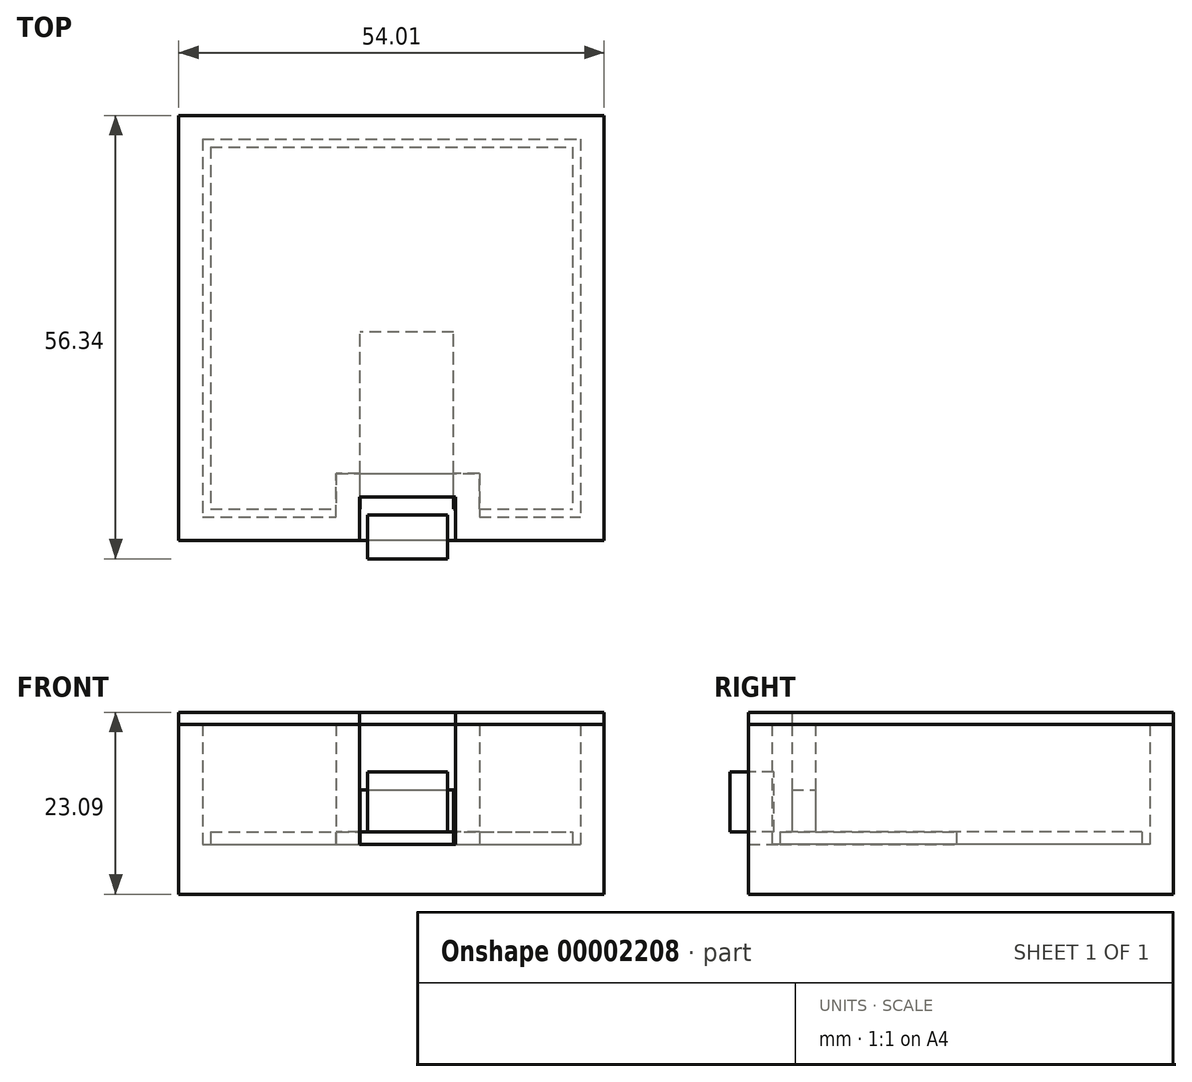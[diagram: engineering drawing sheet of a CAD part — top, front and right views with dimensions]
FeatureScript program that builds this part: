
annotation { "Feature Type Name" : "Feature", "Feature Type Description" : "" }
export const myFeature = defineFeature(function(context is Context, id is Id, definition is map)
    precondition{}
    {
        {
            var Q0;
            Q0=qCreatedBy(makeId("Top.planeOp"),FACE);
            var sketch = newSketch(context, id + "F0", { "sketchPlane" : qUnion([Q0])});
            skLineSegment(sketch, "E0.bottom", {"start": v(-26.57, 18.84) * mm, "end": v(19.4, 18.84) * mm});
            skLineSegment(sketch, "E0.top", {"start": v(-26.57, -27.13) * mm, "end": v(19.4, -27.13) * mm});
            skLineSegment(sketch, "E0.left", {"start": v(-26.57, 18.84) * mm, "end": v(-26.57, -27.13) * mm});
            skLineSegment(sketch, "E0.right", {"start": v(19.4, 18.84) * mm, "end": v(19.4, -27.13) * mm});
            skSolve(sketch);
        }
        {
            var Q0;
            Q0 = qSketchRegion(id + "F0", true);
            extrude(context, id + "F1", {"entities" : qUnion([Q0]), "depth" : 1.57 * mm});
        }
        {
            var Q0;
            Q0=makeQuery(id+"F1.opExtrude","CAP_FACE",FACE,{"disambiguationData":[OSD([sQuery(id+"F0.wireOp",EDGE,"E0.bottom"),sQuery(id+"F0.wireOp",EDGE,"E0.top"),sQuery(id+"F0.wireOp",EDGE,"E0.left"),sQuery(id+"F0.wireOp",EDGE,"E0.right")])],"isStart":false});
            var sketch = newSketch(context, id + "F2", { "sketchPlane" : qUnion([Q0])});
            skLineSegment(sketch, "E1.bottom", {"start": v(-6.59, -23.32) * mm, "end": v(3.57, -23.32) * mm});
            skLineSegment(sketch, "E1.top", {"start": v(-6.59, -33.48) * mm, "end": v(3.57, -33.48) * mm});
            skLineSegment(sketch, "E1.left", {"start": v(-6.59, -23.32) * mm, "end": v(-6.59, -33.48) * mm});
            skLineSegment(sketch, "E1.right", {"start": v(3.57, -23.32) * mm, "end": v(3.57, -33.48) * mm});
            skSolve(sketch);
        }
        {
            var Q0;
            Q0 = qSketchRegion(id + "F2", true);
            extrude(context, id + "F3", {"entities" : qUnion([Q0]), "operationType" : NewBodyOperationType.ADD, "depth" : 7.62 * mm});
        }
        {
            var Q0;
            Q0=makeQuery(id+"F3.opExtrude","CAP_FACE",FACE,{"disambiguationData":[OSD([sQuery(id+"F2.wireOp",EDGE,"E1.bottom"),sQuery(id+"F2.wireOp",EDGE,"E1.top"),sQuery(id+"F2.wireOp",EDGE,"E1.left"),sQuery(id+"F2.wireOp",EDGE,"E1.right")])],"isStart":false});
            var sketch = newSketch(context, id + "F4", { "sketchPlane" : qUnion([Q0])});
            skLineSegment(sketch, "E2.bottom", {"start": v(-6.59, -23.32) * mm, "end": v(3.57, -23.32) * mm});
            skLineSegment(sketch, "E2.top", {"start": v(-6.59, -27.9) * mm, "end": v(3.57, -27.9) * mm});
            skLineSegment(sketch, "E2.left", {"start": v(-6.59, -23.32) * mm, "end": v(-6.59, -27.9) * mm});
            skLineSegment(sketch, "E2.right", {"start": v(3.57, -23.32) * mm, "end": v(3.57, -27.9) * mm});
            skSolve(sketch);
        }
        {
            var Q0;
            Q0 = qSketchRegion(id + "F4", true);
            extrude(context, id + "F5", {"entities" : qUnion([Q0]), "operationType" : NewBodyOperationType.REMOVE, "oppositeDirection" : true, "depth" : 2.3 * mm});
        }
        {
            var Q0;
            Q0=qCreatedBy(makeId("Top.planeOp"),FACE);
            var sketch = newSketch(context, id + "F6", { "sketchPlane" : qUnion([Q0])});
            skLineSegment(sketch, "E3.bottom", {"start": v(-27.59, 19.86) * mm, "end": v(20.42, 19.86) * mm});
            skLineSegment(sketch, "E3.top", {"start": v(-27.59, -28.15) * mm, "end": v(20.42, -28.15) * mm});
            skLineSegment(sketch, "E3.left", {"start": v(-27.59, 19.86) * mm, "end": v(-27.59, -28.15) * mm});
            skLineSegment(sketch, "E3.right", {"start": v(20.42, 19.86) * mm, "end": v(20.42, -28.15) * mm});
            skLineSegment(sketch, "E4.bottom", {"start": v(-30.59, 22.86) * mm, "end": v(23.42, 22.86) * mm});
            skLineSegment(sketch, "E4.top", {"start": v(-30.59, -31.15) * mm, "end": v(23.42, -31.15) * mm});
            skLineSegment(sketch, "E4.left", {"start": v(-30.59, 22.86) * mm, "end": v(-30.59, -31.15) * mm});
            skLineSegment(sketch, "E4.right", {"start": v(23.42, 22.86) * mm, "end": v(23.42, -31.15) * mm});
            skLineSegment(sketch, "E5", {"start": v(-7.6, -28.15) * mm, "end": v(-7.6, -25.6) * mm});
            skLineSegment(sketch, "E6", {"start": v(-7.6, -25.6) * mm, "end": v(4.59, -25.6) * mm});
            skLineSegment(sketch, "E7", {"start": v(4.59, -25.6) * mm, "end": v(4.59, -28.15) * mm});
            skLineSegment(sketch, "E8", {"start": v(-10.6, -28.15) * mm, "end": v(-10.6, -22.6) * mm});
            skLineSegment(sketch, "E9", {"start": v(-10.6, -22.6) * mm, "end": v(7.59, -22.6) * mm});
            skLineSegment(sketch, "E10", {"start": v(7.59, -22.6) * mm, "end": v(7.59, -28.15) * mm});
            skLineSegment(sketch, "E11", {"start": v(-10.6, -28.15) * mm, "end": v(-10.6, -31.15) * mm});
            skLineSegment(sketch, "E12", {"start": v(-7.6, -28.15) * mm, "end": v(-7.6, -31.15) * mm});
            skLineSegment(sketch, "E13", {"start": v(4.59, -28.15) * mm, "end": v(4.59, -31.15) * mm});
            skLineSegment(sketch, "E14", {"start": v(7.59, -28.15) * mm, "end": v(7.59, -31.15) * mm});
            skSolve(sketch);
        }
        {
            var Q0;
            {var subQ2=sQuery(id+"F6.wireOp",EDGE,"E5");Q0=makeQuery(id+"F6.imprint","IMPRINT",FACE,{"disambiguationData":[TD([[makeQuery(id+"F6.imprint","IMPRINT",EDGE,{"derivedFrom":subQ2}),1.0]])]});}
            var Q1;
            Q1=makeQuery(id+"F6.imprint","IMPRINT",FACE,{"disambiguationData":[TD([[makeQuery(id+"F6.imprint","IMPRINT",EDGE,{"derivedFrom":sQuery(id+"F6.wireOp",EDGE,"E3.bottom")}),1.0]])]});
            var Q2;
            {var subQ1=sQuery(id+"F6.wireOp",EDGE,"E11");Q2=makeQuery(id+"F6.imprint","IMPRINT",FACE,{"disambiguationData":[TD([[makeQuery(id+"F6.imprint","IMPRINT",EDGE,{"derivedFrom":subQ1}),1.0]])]});}
            var Q3;
            {var subQ0=sQuery(id+"F6.wireOp",EDGE,"E13");Q3=makeQuery(id+"F6.imprint","IMPRINT",FACE,{"disambiguationData":[TD([[makeQuery(id+"F6.imprint","IMPRINT",EDGE,{"derivedFrom":subQ0}),1.0]])]});}
            extrude(context, id + "F7", {"entities" : qUnion([Q0, Q1, Q2, Q3]), "depth" : 15.24 * mm});
        }
        {
            var Q0;
            Q0=makeQuery(id+"F7.boolean.opBoolean","MERGE",FACE,{"derivedFrom":[makeQuery(id+"F1.opExtrude","CAP_FACE",FACE,{"disambiguationData":[OSD([sQuery(id+"F0.wireOp",EDGE,"E0.bottom"),sQuery(id+"F0.wireOp",EDGE,"E0.top"),sQuery(id+"F0.wireOp",EDGE,"E0.left"),sQuery(id+"F0.wireOp",EDGE,"E0.right")])],"isStart":true}),makeQuery(id+"F7.opExtrude","CAP_FACE",FACE,{"disambiguationData":[OSD([sQuery(id+"F6.wireOp",EDGE,"E3.bottom"),sQuery(id+"F6.wireOp",EDGE,"E3.top"),sQuery(id+"F6.wireOp",EDGE,"E3.left"),sQuery(id+"F6.wireOp",EDGE,"E3.right"),sQuery(id+"F6.wireOp",EDGE,"E4.bottom"),sQuery(id+"F6.wireOp",EDGE,"E4.top"),sQuery(id+"F6.wireOp",EDGE,"E4.left"),sQuery(id+"F6.wireOp",EDGE,"E4.right"),sQuery(id+"F6.wireOp",EDGE,"E5"),sQuery(id+"F6.wireOp",EDGE,"E6"),sQuery(id+"F6.wireOp",EDGE,"E7"),sQuery(id+"F6.wireOp",EDGE,"E8"),sQuery(id+"F6.wireOp",EDGE,"E9"),sQuery(id+"F6.wireOp",EDGE,"E10"),sQuery(id+"F6.wireOp",EDGE,"E12"),sQuery(id+"F6.wireOp",EDGE,"E13")])],"isStart":true})]});
            var sketch = newSketch(context, id + "F8", { "sketchPlane" : qUnion([Q0])});
            skLineSegment(sketch, "E15.bottom", {"start": v(23.42, -22.86) * mm, "end": v(-30.59, -22.86) * mm});
            skLineSegment(sketch, "E15.top", {"start": v(23.42, 31.15) * mm, "end": v(-30.59, 31.15) * mm});
            skLineSegment(sketch, "E15.left", {"start": v(23.42, -22.86) * mm, "end": v(23.42, 31.15) * mm});
            skLineSegment(sketch, "E15.right", {"start": v(-30.59, -22.86) * mm, "end": v(-30.59, 31.15) * mm});
            skSolve(sketch);
        }
        {
            var Q0;
            Q0 = qSketchRegion(id + "F8", true);
            extrude(context, id + "F9", {"entities" : qUnion([Q0]), "operationType" : NewBodyOperationType.ADD, "depth" : 6.35 * mm});
        }
        {
            var Q0;
            Q0=makeQuery(id+"F7.opExtrude","CAP_FACE",FACE,{"disambiguationData":[OSD([sQuery(id+"F6.wireOp",EDGE,"E3.bottom"),sQuery(id+"F6.wireOp",EDGE,"E3.top"),sQuery(id+"F6.wireOp",EDGE,"E3.left"),sQuery(id+"F6.wireOp",EDGE,"E3.right"),sQuery(id+"F6.wireOp",EDGE,"E4.bottom"),sQuery(id+"F6.wireOp",EDGE,"E4.top"),sQuery(id+"F6.wireOp",EDGE,"E4.left"),sQuery(id+"F6.wireOp",EDGE,"E4.right"),sQuery(id+"F6.wireOp",EDGE,"E5"),sQuery(id+"F6.wireOp",EDGE,"E6"),sQuery(id+"F6.wireOp",EDGE,"E7"),sQuery(id+"F6.wireOp",EDGE,"E8"),sQuery(id+"F6.wireOp",EDGE,"E9"),sQuery(id+"F6.wireOp",EDGE,"E10"),sQuery(id+"F6.wireOp",EDGE,"E12"),sQuery(id+"F6.wireOp",EDGE,"E13")])],"isStart":false});
            var sketch = newSketch(context, id + "F10", { "sketchPlane" : qUnion([Q0])});
            skLineSegment(sketch, "E16", {"start": v(-30.59, 22.86) * mm, "end": v(-30.59, -31.15) * mm});
            skLineSegment(sketch, "E17", {"start": v(-30.59, -31.15) * mm, "end": v(-7.6, -31.15) * mm});
            skLineSegment(sketch, "E18", {"start": v(-7.6, -31.15) * mm, "end": v(-7.6, -25.6) * mm});
            skLineSegment(sketch, "E19", {"start": v(-7.6, -25.6) * mm, "end": v(4.59, -25.6) * mm});
            skLineSegment(sketch, "E20", {"start": v(4.59, -25.6) * mm, "end": v(4.59, -31.15) * mm});
            skLineSegment(sketch, "E21", {"start": v(4.59, -31.15) * mm, "end": v(23.42, -31.15) * mm});
            skLineSegment(sketch, "E22", {"start": v(23.42, -31.15) * mm, "end": v(23.42, 22.86) * mm});
            skLineSegment(sketch, "E23", {"start": v(23.42, 22.86) * mm, "end": v(-30.59, 22.86) * mm});
            skSolve(sketch);
        }
        {
            var Q0;
            Q0 = qSketchRegion(id + "F10", true);
            extrude(context, id + "F11", {"entities" : qUnion([Q0]), "depth" : 1.5 * mm});
        }
        {
            var Q0;
            Q0=makeQuery(id+"F5.boolean.opBoolean","COPY",FACE,{"derivedFrom":makeQuery(id+"F5.opExtrude","CAP_FACE",FACE,{"disambiguationData":[OSD([sQuery(id+"F4.wireOp",EDGE,"E2.bottom"),sQuery(id+"F4.wireOp",EDGE,"E2.top"),sQuery(id+"F4.wireOp",EDGE,"E2.left"),sQuery(id+"F4.wireOp",EDGE,"E2.right")])],"isStart":false})});
            var sketch = newSketch(context, id + "F12", { "sketchPlane" : qUnion([Q0])});
            skLineSegment(sketch, "E24.bottom", {"start": v(4.32, -27.9) * mm, "end": v(-7.56, -27.9) * mm});
            skLineSegment(sketch, "E24.top", {"start": v(4.32, -4.66) * mm, "end": v(-7.56, -4.66) * mm});
            skLineSegment(sketch, "E24.left", {"start": v(4.32, -27.9) * mm, "end": v(4.32, -4.66) * mm});
            skLineSegment(sketch, "E24.right", {"start": v(-7.56, -27.9) * mm, "end": v(-7.56, -4.66) * mm});
            skSolve(sketch);
        }
        {
            var Q0;
            Q0 = qSketchRegion(id + "F12", true);
            extrude(context, id + "F13", {"entities" : qUnion([Q0]), "operationType" : NewBodyOperationType.REMOVE, "oppositeDirection" : true, "depth" : 6.9 * mm});
        }
    });
